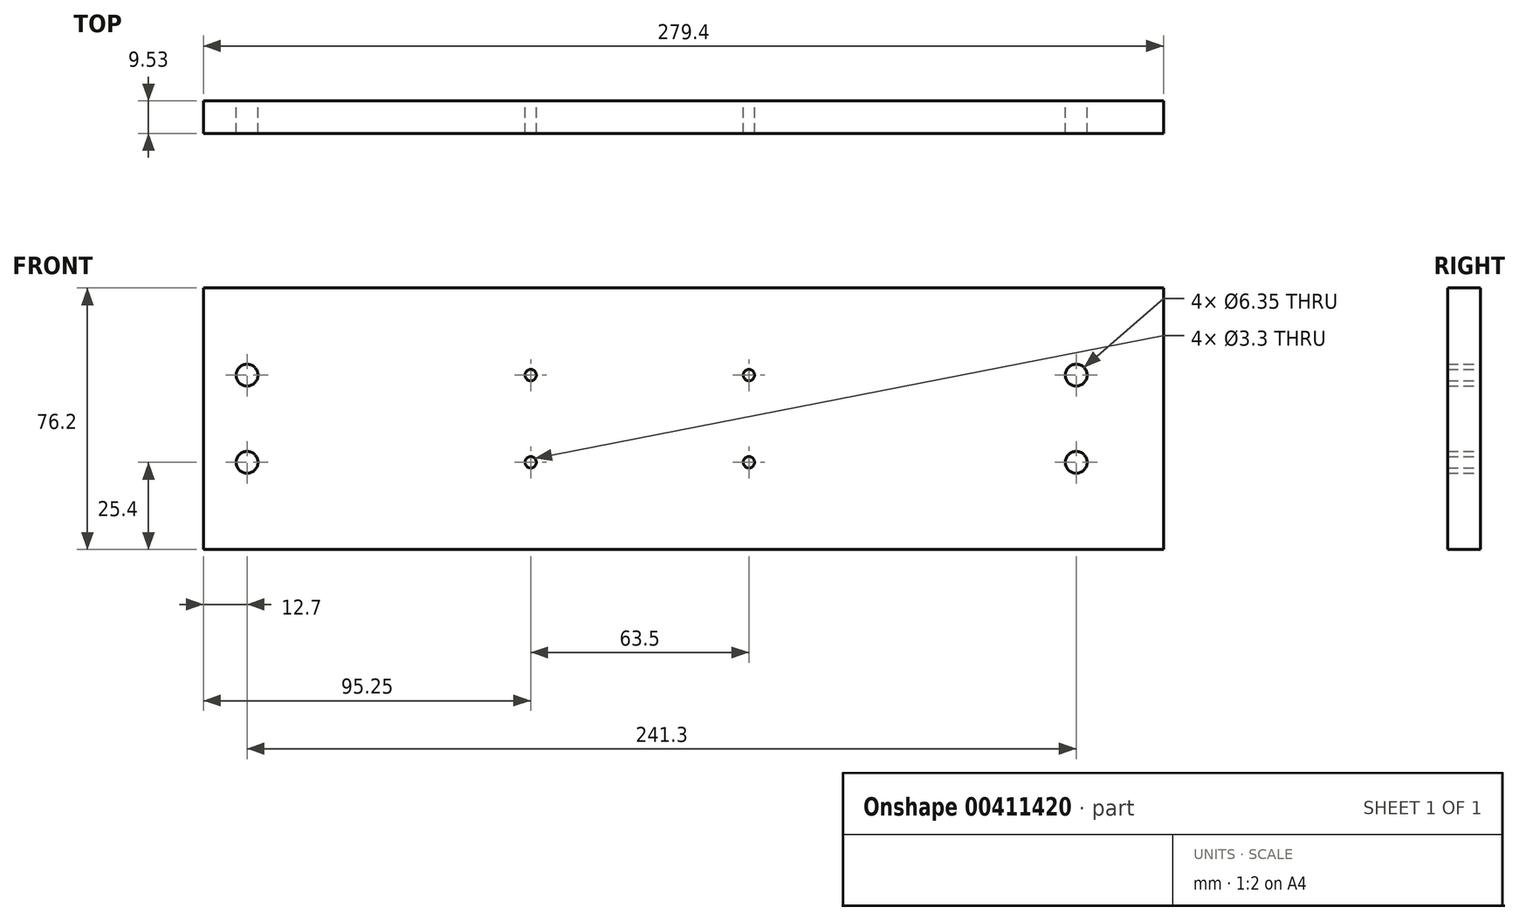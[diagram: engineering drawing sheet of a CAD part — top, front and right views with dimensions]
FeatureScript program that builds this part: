
annotation { "Feature Type Name" : "Feature", "Feature Type Description" : "" }
export const myFeature = defineFeature(function(context is Context, id is Id, definition is map)
    precondition{}
    {
        {
            var Q0;
            Q0=qCreatedBy(makeId("Front.planeOp"),FACE);
            var sketch = newSketch(context, id + "F0", { "sketchPlane" : qUnion([Q0])});
            skLineSegment(sketch, "E0.bottom", {"start": v(0, 76.2) * mm, "end": v(279.4, 76.2) * mm});
            skLineSegment(sketch, "E0.top", {"start": v(0, 0) * mm, "end": v(279.4, 0) * mm});
            skLineSegment(sketch, "E0.left", {"start": v(0, 76.2) * mm, "end": v(0, 0) * mm});
            skLineSegment(sketch, "E0.right", {"start": v(279.4, 76.2) * mm, "end": v(279.4, 0) * mm});
            skCircle(sketch, "E1", {"center": v(12.7, 50.8) * mm, "radius": 3.18 * mm});
            skCircle(sketch, "E2", {"center": v(12.7, 25.4) * mm, "radius": 3.18 * mm});
            skCircle(sketch, "E3", {"center": v(254, 50.8) * mm, "radius": 3.18 * mm});
            skCircle(sketch, "E4", {"center": v(254, 25.4) * mm, "radius": 3.18 * mm});
            skCircle(sketch, "E5", {"center": v(95.25, 50.8) * mm, "radius": 1.65 * mm});
            skCircle(sketch, "E6", {"center": v(95.25, 25.4) * mm, "radius": 1.65 * mm});
            skCircle(sketch, "E7", {"center": v(158.75, 50.8) * mm, "radius": 1.65 * mm});
            skCircle(sketch, "E8", {"center": v(158.75, 25.4) * mm, "radius": 1.65 * mm});
            skSolve(sketch);
        }
        {
            var Q0;
            Q0 = qSketchRegion(id + "F0", true);
            extrude(context, id + "F1", {"entities" : qUnion([Q0]), "depth" : 9.52 * mm});
        }
    });
